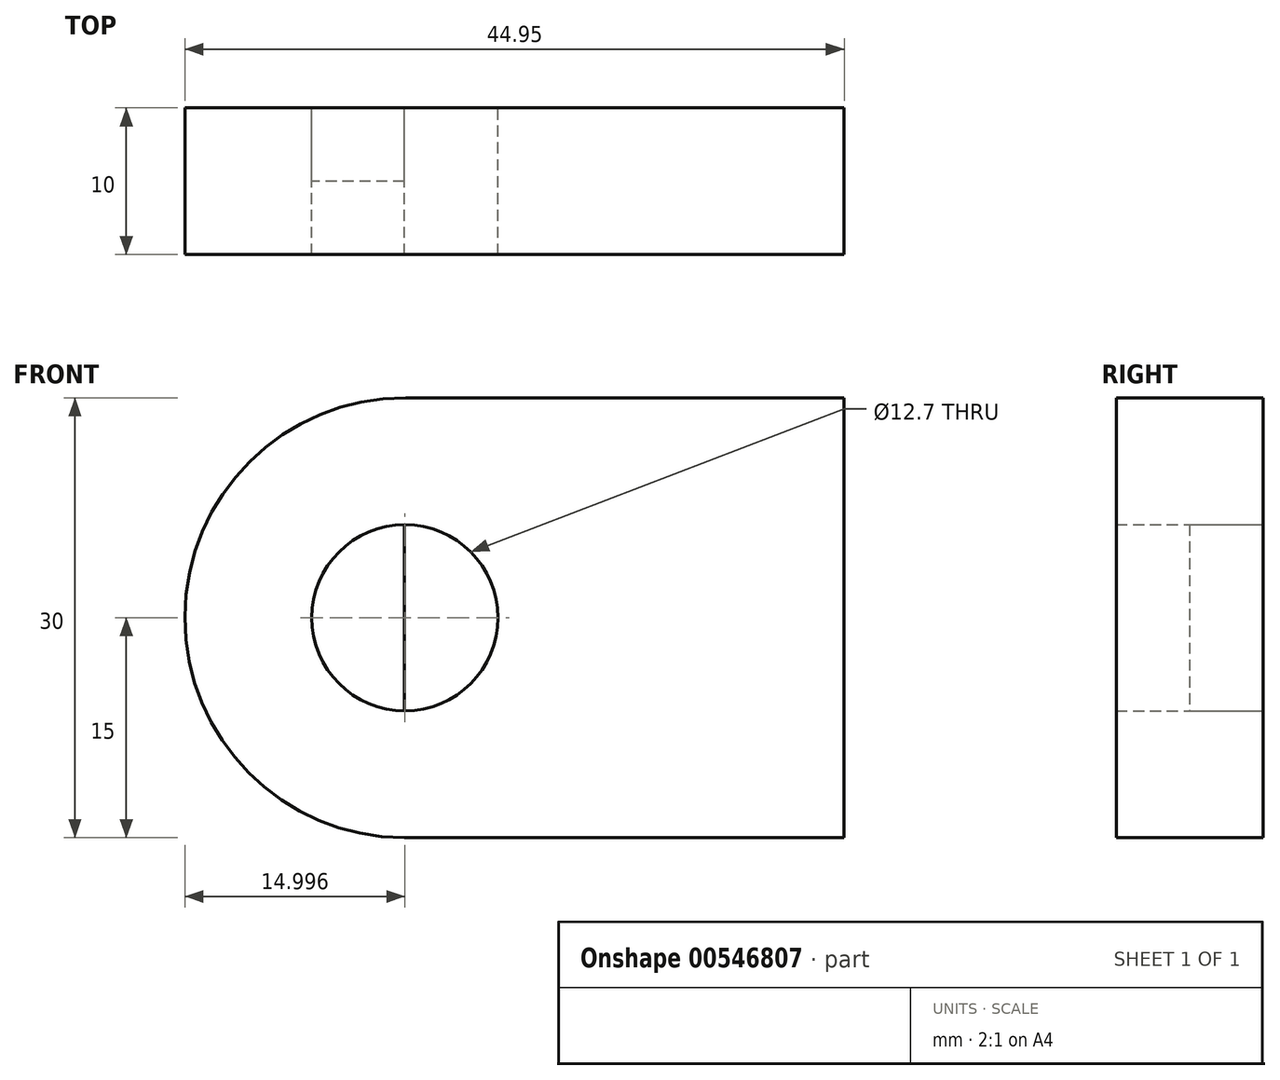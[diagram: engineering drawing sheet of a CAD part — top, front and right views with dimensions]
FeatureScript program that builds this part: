
annotation { "Feature Type Name" : "Feature", "Feature Type Description" : "" }
export const myFeature = defineFeature(function(context is Context, id is Id, definition is map)
    precondition{}
    {
        {
            var Q0;
            Q0=qCreatedBy(makeId("Front.planeOp"),FACE);
            var sketch = newSketch(context, id + "F0", { "sketchPlane" : qUnion([Q0])});
            skCircle(sketch, "E0", {"center": v(-21.05, 0) * mm, "radius": 6.35 * mm});
            skCircle(sketch, "E1", {"center": v(-21.05, 0) * mm, "radius": 15 * mm});
            skLineSegment(sketch, "E2.bottom", {"start": v(-21.1, 15) * mm, "end": v(8.9, 15) * mm});
            skLineSegment(sketch, "E2.top", {"start": v(-21.1, -15) * mm, "end": v(8.9, -15) * mm});
            skLineSegment(sketch, "E2.left", {"start": v(-21.1, 15) * mm, "end": v(-21.1, -15) * mm});
            skLineSegment(sketch, "E2.right", {"start": v(8.9, 15) * mm, "end": v(8.9, -15) * mm});
            skSolve(sketch);
        }
        {
            var Q0;
            Q0 = qSketchRegion(id + "F0", true);
            extrude(context, id + "F1", {"entities" : qUnion([Q0]), "depth" : 10 * mm, "offsetDistance" : 25.4 * mm});
        }
        {
            var Q0;
            {var subQ0=sQuery(id+"F0.wireOp",EDGE,"E2.left");var subQ1=sQuery(id+"F0.wireOp",EDGE,"E0");var subQ2=makeQuery(id+"F0.imprint","INTERSECT",VERTEX,{"disambiguationData":[OD(0.0)],"derivedFrom":[subQ1,subQ0]});Q0=makeQuery(id+"F0.imprint","IMPRINT",FACE,{"disambiguationData":[TD([[makeQuery(id+"F0.imprint","IMPRINT",EDGE,{"disambiguationData":[TD([[subQ2,-1.0]])],"derivedFrom":subQ1}),1.0]])]});}
            extrude(context, id + "F2", {"entities" : qUnion([Q0]), "depth" : 5 * mm, "offsetDistance" : 25.4 * mm});
        }
    });
